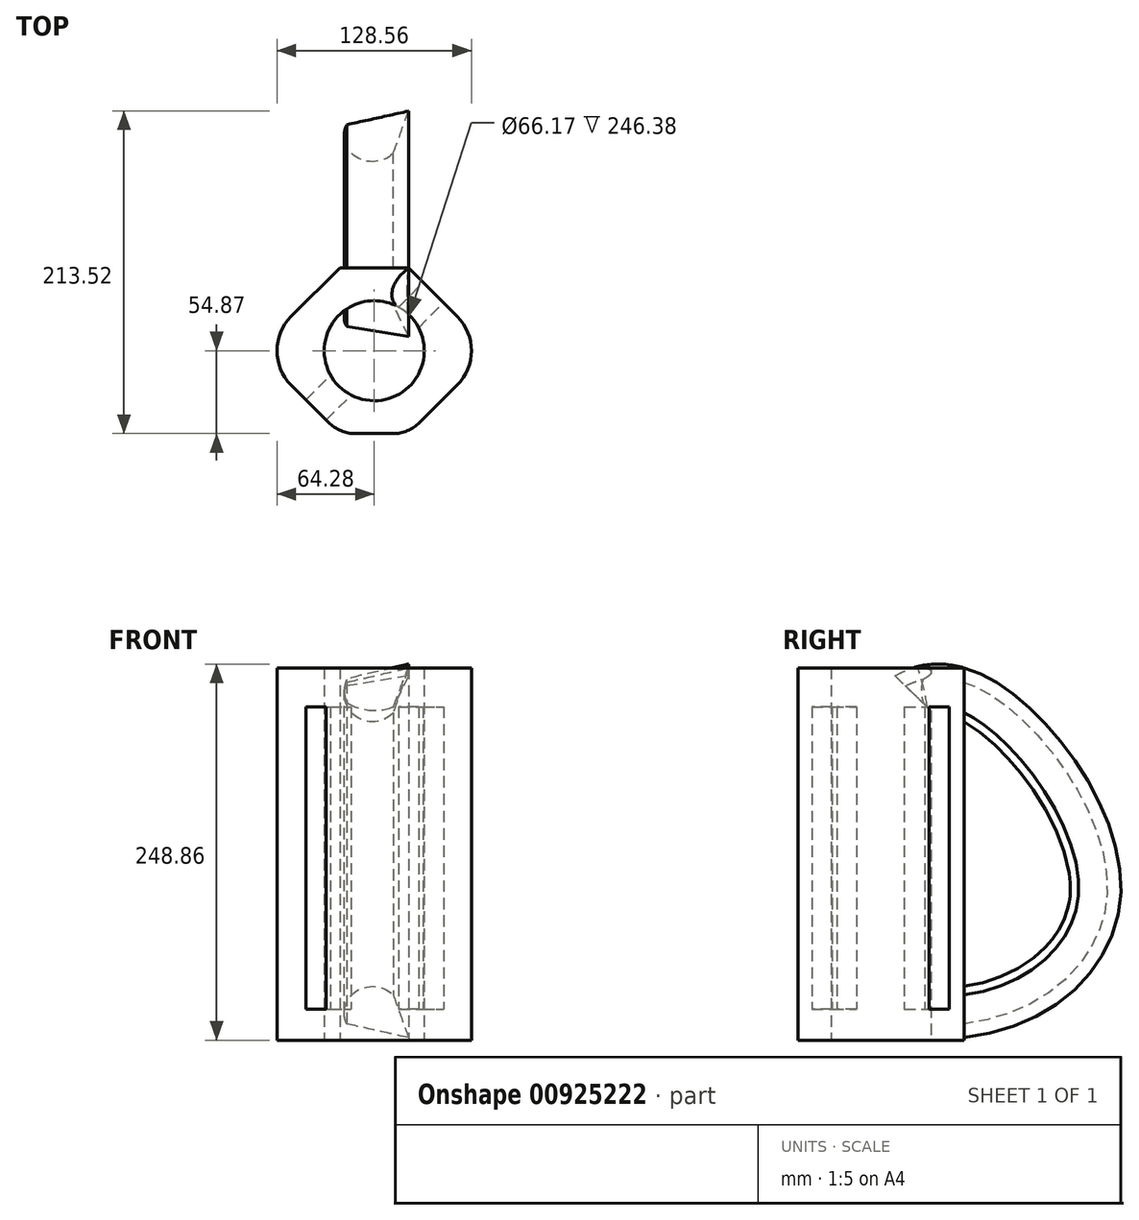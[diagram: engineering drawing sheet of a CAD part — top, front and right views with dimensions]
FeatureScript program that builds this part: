
annotation { "Feature Type Name" : "Feature", "Feature Type Description" : "" }
export const myFeature = defineFeature(function(context is Context, id is Id, definition is map)
    precondition{}
    {
        {
            var Q0;
            Q0=qCreatedBy(makeId("Top.planeOp"),FACE);
            var sketch = newSketch(context, id + "F0", { "sketchPlane" : qUnion([Q0])});
            skCircle(sketch, "E0.cCircle", {"center": v(0, 0) * mm, "radius": 54.87 * mm, "construction": true});
            skLineSegment(sketch, "E0.0", {"start": v(54.87, 22.73) * mm, "end": v(54.87, -22.73) * mm});
            skLineSegment(sketch, "E0.1", {"start": v(54.87, -22.73) * mm, "end": v(22.73, -54.87) * mm});
            skLineSegment(sketch, "E0.2", {"start": v(22.73, -54.87) * mm, "end": v(-22.73, -54.87) * mm});
            skLineSegment(sketch, "E0.3", {"start": v(-22.73, -54.87) * mm, "end": v(-54.87, -22.73) * mm});
            skLineSegment(sketch, "E0.4", {"start": v(-54.87, -22.73) * mm, "end": v(-54.87, 22.73) * mm});
            skLineSegment(sketch, "E0.5", {"start": v(-54.87, 22.73) * mm, "end": v(-22.73, 54.87) * mm});
            skLineSegment(sketch, "E0.6", {"start": v(-22.73, 54.87) * mm, "end": v(22.73, 54.87) * mm});
            skLineSegment(sketch, "E0.7", {"start": v(22.73, 54.87) * mm, "end": v(54.87, 22.73) * mm});
            skPoint(sketch, "E0.0.midPoint", {"position": v(54.87, 0) * mm});
            skArc(sketch, "E1", {"start": v(-54.87, 22.73) * mm, "mid": v(-64.28, 0) * mm, "end": v(-54.87, -22.73) * mm});
            skArc(sketch, "E2", {"start": v(54.87, -22.73) * mm, "mid": v(64.28, 0) * mm, "end": v(54.87, 22.73) * mm});
            skCircle(sketch, "E3", {"center": v(0, 0) * mm, "radius": 33.09 * mm});
            skSolve(sketch);
        }
        {
            var Q0;
            Q0 = qSketchRegion(id + "F0", true);
            extrude(context, id + "F1", {"entities" : qUnion([Q0]), "depth" : 246.38 * mm, "offsetDistance" : 25.4 * mm});
        }
        {
            var Q0;
            Q0=makeQuery(id+"F1.opExtrude","SWEPT_FACE",FACE,{"disambiguationData":[OSD([sQuery(id+"F0.wireOp",EDGE,"E0.7")])]});
            var sketch = newSketch(context, id + "F2", { "sketchPlane" : qUnion([Q0])});
            skLineSegment(sketch, "E4.bottom", {"start": v(8.99, 220.69) * mm, "end": v(-10, 220.69) * mm});
            skLineSegment(sketch, "E4.top", {"start": v(8.99, 20.5) * mm, "end": v(-10, 20.5) * mm});
            skLineSegment(sketch, "E4.left", {"start": v(8.99, 220.69) * mm, "end": v(8.99, 20.5) * mm});
            skLineSegment(sketch, "E4.right", {"start": v(-10, 220.69) * mm, "end": v(-10, 20.5) * mm});
            skSolve(sketch);
        }
        {
            var Q0;
            Q0=makeQuery(id+"F2.imprint","IMPRINT",FACE,{"disambiguationData":[TD([[makeQuery(id+"F2.imprint","IMPRINT",EDGE,{"derivedFrom":sQuery(id+"F2.wireOp",EDGE,"E4.bottom")}),1.0]])]});
            var Q1;
            Q1=makeQuery(id+"F1.opExtrude","SWEPT_FACE",FACE,{"disambiguationData":[OSD([sQuery(id+"F0.wireOp",EDGE,"E0.3")])]});
            extrude(context, id + "F3", {"entities" : qUnion([Q0]), "operationType" : NewBodyOperationType.REMOVE, "endBound" : BoundingType.UP_TO_SURFACE, "oppositeDirection" : true, "depth" : 25.4 * mm, "endBoundEntityFace" : qUnion([Q1]), "offsetDistance" : 25.4 * mm});
        }
        {
            var Q0;
            Q0=makeQuery(id+"F1.opExtrude","SWEPT_FACE",FACE,{"disambiguationData":[OSD([sQuery(id+"F0.wireOp",EDGE,"E0.6")])]});
            var sketch = newSketch(context, id + "F4", { "sketchPlane" : qUnion([Q0])});
            skLineSegment(sketch, "E5.bottom", {"start": v(-22.73, 246.38) * mm, "end": v(18.2, 236.84) * mm});
            skLineSegment(sketch, "E5.left", {"start": v(-22.73, 246.38) * mm, "end": v(-12.56, 216.76) * mm});
            skLineSegment(sketch, "E6", {"start": v(-12.56, 216.76) * mm, "end": v(18.2, 236.84) * mm});
            skArc(sketch, "E7", {"start": v(-12.56, 216.76) * mm, "mid": v(11.37, 213.7) * mm, "end": v(18.2, 236.84) * mm});
            skSolve(sketch);
        }
        {
            var Q0;
            Q0=qCreatedBy(makeId("Right.planeOp"),FACE);
            var sketch = newSketch(context, id + "F5", { "sketchPlane" : qUnion([Q0])});
            skFitSpline(sketch, "E8", {"points": [v(17.1, 233.47) * mm, v(71.99, 227.25) * mm, v(148.12, 96.74) * mm, v(45.58, 11.29) * mm], "startDerivative": vector(180.06, 93.68) * mm, "endDerivative": vector(-465.7, -26.48) * mm});
            skSolve(sketch);
        }
        {
            var Q0;
            Q0=makeQuery(id+"F4.imprint","IMPRINT",FACE,{"disambiguationData":[TD([[makeQuery(id+"F4.imprint","IMPRINT",EDGE,{"derivedFrom":sQuery(id+"F4.wireOp",EDGE,"E5.bottom")}),-1.0]])]});
            var Q1;
            Q1=makeQuery(id+"F4.imprint","IMPRINT",FACE,{"disambiguationData":[TD([[makeQuery(id+"F4.imprint","IMPRINT",EDGE,{"derivedFrom":sQuery(id+"F4.wireOp",EDGE,"E6")}),-1.0]])]});
            var Q2;
            Q2=sQuery(id+"F5.wireOp",EDGE,"E8");
            sweep(context, id + "F6", {"operationType" : NewBodyOperationType.ADD, "profiles" : qUnion([Q0, Q1]), "path" : qUnion([Q2])});
        }
        {
            var Q0;
            Q0=makeQuery(id+"F1.opExtrude","SWEPT_EDGE",EDGE,{"disambiguationData":[OSD([sQuery(id+"F0.wireOp",EDGE,"E0.1"),sQuery(id+"F0.wireOp",EDGE,"E0.2")])]});
            var Q1;
            Q1=makeQuery(id+"F1.opExtrude","SWEPT_EDGE",EDGE,{"disambiguationData":[OSD([sQuery(id+"F0.wireOp",EDGE,"E0.2"),sQuery(id+"F0.wireOp",EDGE,"E0.3")])]});
            fillet(context, id + "F7", {"entities" : qUnion([Q0, Q1]), "radius" : 25.4 * mm, "tangentPropagation" : true, "allowEdgeOverflow" : false});
        }
    });
